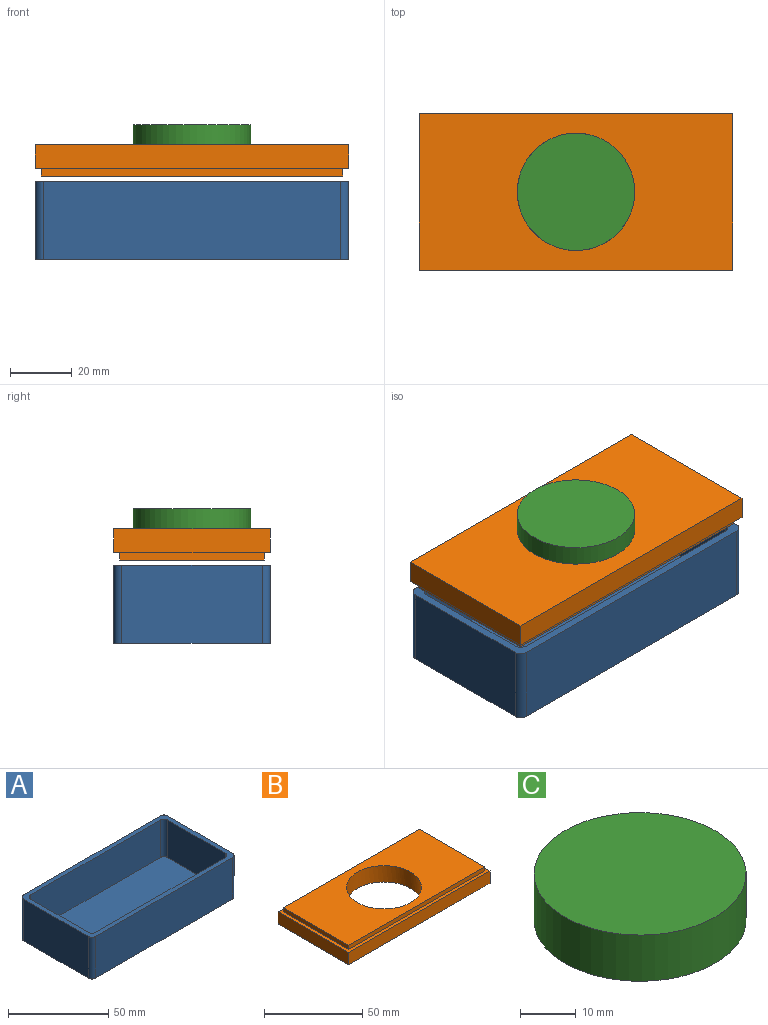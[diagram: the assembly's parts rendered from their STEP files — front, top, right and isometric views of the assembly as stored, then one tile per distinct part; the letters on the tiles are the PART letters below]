
ASSEMBLY  parts=3 mates=3
PART A: 19 faces, bbox 101.6x50.8x25.4 mm
  f0: plane 101.6x50.8mm, normal (0,0,1), area 748.4mm2, adj f1,f2,f3,f4,f6,f7,f8,f9
  f1: plane 45.72x25.4mm, normal (1,0,0), area 1161.3mm2, adj f0,f5,f15,f18
  f2: plane 96.52x25.4mm, normal (0,1,0), area 2451.6mm2, adj f0,f5,f15,f16
  f3: plane 45.72x25.4mm, normal (-1,0,0), area 1161.3mm2, adj f0,f5,f16,f17
  f4: plane 96.52x25.4mm, normal (0,-1,0), area 2451.6mm2, adj f0,f5,f17,f18
  f5: plane 101.6x50.8mm, normal (0,0,-1), area 5155.7mm2, adj f1,f2,f3,f4,f15,f16,f17,f18
  f6: plane 40.64x22.86mm, normal (-1,0,0), area 929mm2, adj f0,f10,f12,f14
  f7: plane 91.44x22.86mm, normal (0,-1,0), area 2090.3mm2, adj f0,f10,f13,f14
  f8: plane 40.64x22.86mm, normal (1,0,0), area 929mm2, adj f0,f10,f11,f13
  f9: plane 91.44x22.86mm, normal (0,1,0), area 2090.3mm2, adj f0,f10,f11,f12
  f10: plane 96.52x45.72mm, normal (0,0,1), area 4407.4mm2, adj f6,f7,f8,f9,f11,f12,f13,f14
  f11: cylinder r=2.54mm len=22.86mm, axis (0,0,-1), area 91.2mm2, adj f0,f8,f9,f10
  f12: cylinder r=2.54mm len=22.86mm, axis (0,0,1), area 91.2mm2, adj f0,f6,f9,f10
  f13: cylinder r=2.54mm len=22.86mm, axis (0,0,1), area 91.2mm2, adj f0,f7,f8,f10
  f14: cylinder r=2.54mm len=22.86mm, axis (0,0,-1), area 91.2mm2, adj f0,f6,f7,f10
  f15: cylinder r=2.54mm len=25.4mm, axis (0,0,1), area 101.3mm2, adj f0,f1,f2,f5
  f16: cylinder r=2.54mm len=25.4mm, axis (0,0,-1), area 101.3mm2, adj f0,f2,f3,f5
  f17: cylinder r=2.54mm len=25.4mm, axis (0,0,1), area 101.3mm2, adj f0,f3,f4,f5
  f18: cylinder r=2.54mm len=25.4mm, axis (0,0,-1), area 101.3mm2, adj f0,f1,f4,f5
PART B: 12 faces, bbox 101.6x50.8x10.2 mm
  f0: plane 101.6x50.8mm, normal (0,0,1), area 566.1mm2, adj f1,f2,f3,f4,f6,f7,f8,f9
  f1: plane 101.6x7.62mm, normal (0,1,0), area 774.2mm2, adj f0,f2,f4,f5
  f2: plane 50.8x7.62mm, normal (-1,0,0), area 387.1mm2, adj f0,f1,f3,f5
  f3: plane 101.6x7.62mm, normal (0,-1,0), area 774.2mm2, adj f0,f2,f4,f5
  f4: plane 50.8x7.62mm, normal (1,0,0), area 387.1mm2, adj f0,f1,f3,f5
  f5: plane 101.6x50.8mm, normal (0,0,-1), area 4021.2mm2, adj f1,f2,f3,f4,f11
  f6: plane 97.79x2.54mm, normal (0,1,0), area 248.4mm2, adj f0,f7,f9,f10
  f7: plane 46.99x2.54mm, normal (-1,0,0), area 119.4mm2, adj f0,f6,f8,f10
  f8: plane 97.79x2.54mm, normal (0,-1,0), area 248.4mm2, adj f0,f7,f9,f10
  f9: plane 46.99x2.54mm, normal (1,0,0), area 119.4mm2, adj f0,f6,f8,f10
  f10: plane 97.79x46.99mm, normal (0,0,1), area 3455.1mm2, adj f6,f7,f8,f9,f11
  f11: cylinder r=19.05mm len=38.1mm, axis (0,0,-1), area 1216.1mm2, adj f5,f10
PART C: 3 faces, bbox 38.1x38.1x10.2 mm
  f0: cylinder r=19.05mm len=38.1mm, axis (0,0,-1), area 1216.1mm2, adj f1,f2
  f1: plane 38.1x38.1mm, normal (0,0,1), area 1140.1mm2, adj f0
  f2: plane 38.1x38.1mm, normal (0,0,-1), area 1140.1mm2, adj f0
PLACE A t=(-5.98,-9.7,6.82)mm
PLACE B rot(axis=(1,0,0),180deg) t=(-5.98,-9.7,43.98)mm
PLACE C t=(-5.98,-9.7,40.35)mm
MATE planar B.f3 <-> A.f2  axis (0,1,0) through (-5.98,15.7,40.17)mm
MATE slider C.f0 <-> B.f11  axis (0,0,-1) through (-5.98,-9.7,45.43)mm
MATE planar B.f4 <-> A.f1  axis (1,0,0) through (44.82,-9.7,40.17)mm
